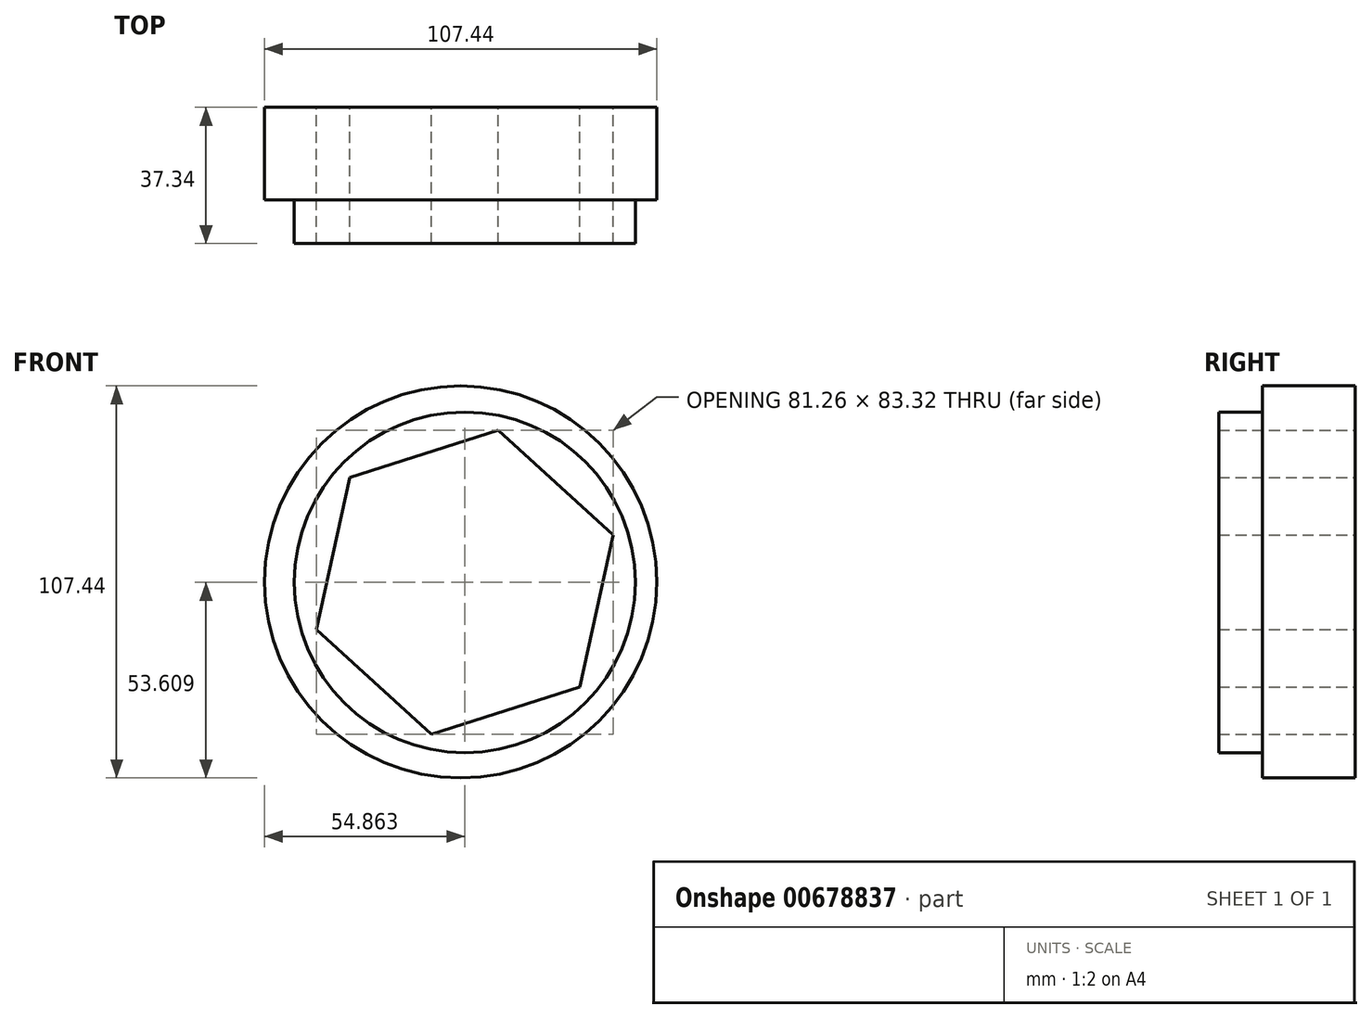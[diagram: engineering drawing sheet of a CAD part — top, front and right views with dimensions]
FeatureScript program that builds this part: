
annotation { "Feature Type Name" : "Feature", "Feature Type Description" : "" }
export const myFeature = defineFeature(function(context is Context, id is Id, definition is map)
    precondition{}
    {
        {
            var Q0;
            Q0=qCreatedBy(makeId("Front.planeOp"),FACE);
            var sketch = newSketch(context, id + "F0", { "sketchPlane" : qUnion([Q0])});
            skCircle(sketch, "E0", {"center": v(0, 0) * mm, "radius": 53.72 * mm});
            skCircle(sketch, "E1", {"center": v(0, 0) * mm, "radius": 58.67 * mm, "construction": true});
            skCircle(sketch, "E2", {"center": v(0, 0) * mm, "radius": 63.5 * mm, "construction": true});
            skLineSegment(sketch, "E3", {"start": v(0, 0) * mm, "end": v(0, 73.15) * mm, "construction": true});
            skLineSegment(sketch, "E4", {"start": v(0, 0) * mm, "end": v(-4.82, 73.56) * mm, "construction": true});
            skLineSegment(sketch, "E5", {"start": v(0, 58.67) * mm, "end": v(-75.67, 58.67) * mm, "construction": true});
            skLineSegment(sketch, "E6", {"start": v(0, 58.67) * mm, "end": v(-75.48, 31.2) * mm, "construction": true});
            skCircle(sketch, "E7", {"center": v(0, 58.67) * mm, "radius": 22.02 * mm, "construction": true});
            skCircle(sketch, "E8", {"center": v(-20.7, 51.14) * mm, "radius": 22.36 * mm, "construction": true});
            skArc(sketch, "E9", {"start": v(0, 58.67) * mm, "mid": v(-19.58, 80.27) * mm, "end": v(-20.7, 51.14) * mm});
            skArc(sketch, "E10", {"start": v(-16.61, 73.13) * mm, "mid": v(-4.35, 66.4) * mm, "end": v(1.52, 53.7) * mm});
            skArc(sketch, "E11", {"start": v(1.52, 53.7) * mm, "mid": v(0.6, 57.63) * mm, "end": v(-0.83, 61.41) * mm});
            skArc(sketch, "E12.MirrorCS", {"start": v(-8.52, 53.04) * mm, "mid": v(-8.12, 57.06) * mm, "end": v(-7.2, 61) * mm});
            skArc(sketch, "E13", {"start": v(-0.83, 61.41) * mm, "mid": v(-4.15, 63.3) * mm, "end": v(-7.2, 61) * mm});
            skCircle(sketch, "E14", {"center": v(1.14, -0.11) * mm, "radius": 46.69 * mm});
            skCircle(sketch, "E15.cCircle", {"center": v(1.14, -0.11) * mm, "radius": 36.93 * mm, "construction": true});
            skLineSegment(sketch, "E15.0", {"start": v(-30.38, 28.6) * mm, "end": v(10.24, 41.55) * mm});
            skLineSegment(sketch, "E15.1", {"start": v(10.24, 41.55) * mm, "end": v(41.77, 12.84) * mm});
            skLineSegment(sketch, "E15.2", {"start": v(41.77, 12.84) * mm, "end": v(32.67, -28.82) * mm});
            skLineSegment(sketch, "E15.3", {"start": v(32.67, -28.82) * mm, "end": v(-7.96, -41.77) * mm});
            skLineSegment(sketch, "E15.4", {"start": v(-7.96, -41.77) * mm, "end": v(-39.49, -13.06) * mm});
            skLineSegment(sketch, "E15.5", {"start": v(-39.49, -13.06) * mm, "end": v(-30.38, 28.6) * mm});
            skPoint(sketch, "E15.0.midPoint", {"position": v(-10.07, 35.07) * mm});
            skSolve(sketch);
        }
        {
            var Q0;
            {var subQ0=sQuery(id+"F0.wireOp",EDGE,"E0");var subQ2=makeQuery(id+"F0.imprint","INTERSECT",VERTEX,{"derivedFrom":[subQ0,sQuery(id+"F0.wireOp",EDGE,"E12.MirrorCS")]});Q0=makeQuery(id+"F0.imprint","IMPRINT",FACE,{"disambiguationData":[TD([[makeQuery(id+"F0.imprint","IMPRINT",EDGE,{"disambiguationData":[TD([[subQ2,1.0]])],"derivedFrom":subQ0}),1.0]])]});}
            var Q1;
            {var subQ0=sQuery(id+"F0.wireOp",EDGE,"E12.MirrorCS");Q1=makeQuery(id+"F0.imprint","IMPRINT",FACE,{"disambiguationData":[TD([[makeQuery(id+"F0.imprint","IMPRINT",EDGE,{"derivedFrom":subQ0}),-1.0]])]});}
            extrude(context, id + "F1", {"entities" : qUnion([Q0, Q1]), "depth" : 25.4 * mm, "offsetDistance" : 25.4 * mm});
        }
        {
            var Q0;
            Q0=makeQuery(id+"F1.opExtrude","SWEPT_BODY",BODY,{"disambiguationData":[OSD([sQuery(id+"F0.wireOp",EDGE,"E0"),sQuery(id+"F0.wireOp",EDGE,"E11"),sQuery(id+"F0.wireOp",EDGE,"E12.MirrorCS"),sQuery(id+"F0.wireOp",EDGE,"E13")])]});
            var Q1;
            Q1=makeQuery(id+"F1.opExtrude","SWEPT_FACE",FACE,{"disambiguationData":[OSD([sQuery(id+"F0.wireOp",EDGE,"E0")])]});
            circularPattern(context, id + "F2", {"entities" : qUnion([Q0]), "axis" : qUnion([Q1]), "angle" : 360 * degree, "instanceCount" : 24, "equalSpace" : true});
        }
        {
            var Q0;
            Q0=makeQuery(id+"F0.imprint","IMPRINT",FACE,{"disambiguationData":[TD([[makeQuery(id+"F0.imprint","IMPRINT",EDGE,{"derivedFrom":sQuery(id+"F0.wireOp",EDGE,"E15.0")}),-1.0]])]});
            var Q1;
            Q1=makeQuery(id+"F0.imprint","IMPRINT",FACE,{"disambiguationData":[TD([[makeQuery(id+"F0.imprint","IMPRINT",EDGE,{"derivedFrom":sQuery(id+"F0.wireOp",EDGE,"E14")}),1.0]])]});
            extrude(context, id + "F3", {"entities" : qUnion([Q0, Q1]), "operationType" : NewBodyOperationType.ADD, "depth" : 37.34 * mm, "offsetDistance" : 25.4 * mm});
        }
        {
            var Q0;
            Q0=makeQuery(id+"F0.imprint","IMPRINT",FACE,{"disambiguationData":[TD([[makeQuery(id+"F0.imprint","IMPRINT",EDGE,{"derivedFrom":sQuery(id+"F0.wireOp",EDGE,"E15.0")}),-1.0]])]});
            extrude(context, id + "F4", {"entities" : qUnion([Q0]), "operationType" : NewBodyOperationType.REMOVE, "depth" : 103.38 * mm, "offsetDistance" : 25.4 * mm});
        }
    });
